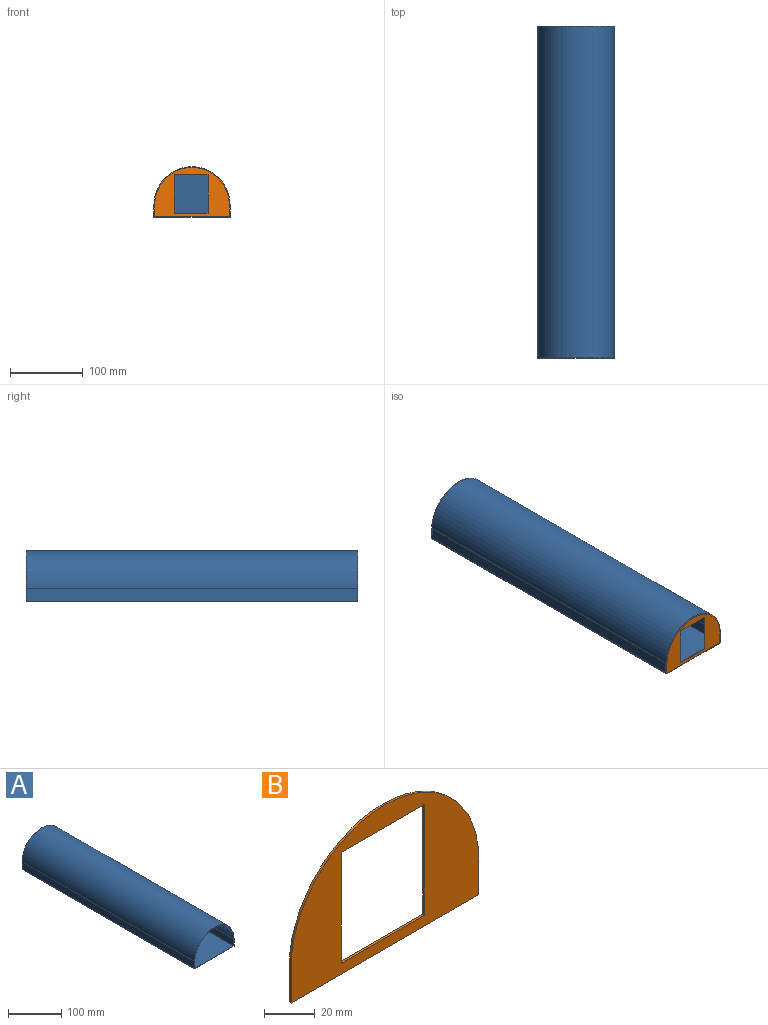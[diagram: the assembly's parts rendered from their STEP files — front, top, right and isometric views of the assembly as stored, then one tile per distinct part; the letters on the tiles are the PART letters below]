
ASSEMBLY  parts=2 mates=1
PART A: 11 faces, bbox 104.7x457.2x69.6 mm
  f0: plane 457.2x17.21mm, normal (1,0,0), area 7869.8mm2, adj f1,f3,f4,f5
  f1: cylinder r=52.35mm len=457.2mm, axis (0,1,0), area 75190.6mm2, adj f0,f2,f4,f5
  f2: plane 457.2x17.21mm, normal (-1,0,0), area 7869.8mm2, adj f1,f3,f4,f5
  f3: plane 457.2x104.7mm, normal (0,0,-1), area 47867.8mm2, adj f0,f2,f4,f5
  f4: plane 104.7x69.56mm, normal (0,-1,0), area 304.8mm2, adj f0,f1,f2,f3,f6,f7,f8,f9
  f5: plane 104.7x69.56mm, normal (0,1,0), area 6106.8mm2, adj f0,f1,f2,f3
  f6: plane 456.18x16.2mm, normal (-1,0,0), area 7388.8mm2, adj f4,f7,f9,f10
  f7: cylinder r=51.33mm len=456.18mm, axis (0,1,0), area 73567.5mm2, adj f4,f6,f8,f10
  f8: plane 456.18x16.2mm, normal (1,0,0), area 7388.8mm2, adj f4,f7,f9,f10
  f9: plane 456.18x102.67mm, normal (0,0,1), area 46834.5mm2, adj f4,f6,f8,f10
  f10: plane 102.67x67.53mm, normal (0,-1,0), area 5802mm2, adj f6,f7,f8,f9
PART B: 10 faces, bbox 104.7x1x69.6 mm
  f0: plane 17.21x1.02mm, normal (-1,0,0), area 17.5mm2, adj f1,f7,f8,f9
  f1: plane 104.7x1.02mm, normal (0,0,-1), area 106.4mm2, adj f0,f2,f8,f9
  f2: plane 17.21x1.02mm, normal (1,0,0), area 17.5mm2, adj f1,f7,f8,f9
  f3: plane 46.48x1.02mm, normal (0,0,-1), area 47.2mm2, adj f4,f6,f8,f9
  f4: plane 53.58x1.02mm, normal (-1,0,0), area 54.4mm2, adj f3,f5,f8,f9
  f5: plane 46.48x1.02mm, normal (0,0,1), area 47.2mm2, adj f4,f6,f8,f9
  f6: plane 53.58x1.02mm, normal (1,0,0), area 54.4mm2, adj f3,f5,f8,f9
  f7: cylinder r=52.35mm len=104.7mm, axis (0,1,0), area 167.1mm2, adj f0,f2,f8,f9
  f8: plane 104.7x69.56mm, normal (0,-1,0), area 3616.7mm2, adj f0,f1,f2,f3,f4,f5,f6,f7
  f9: plane 104.7x69.56mm, normal (0,1,0), area 3616.7mm2, adj f0,f1,f2,f3,f4,f5,f6,f7
PLACE A t=(-405.32,467.78,-549.25)mm
PLACE B t=(-405.32,11.6,-549.2)mm
MATE parallel A.f1 <-> B.f7  axis (0,-1,0) through (-405.32,10.58,-548.98)mm
